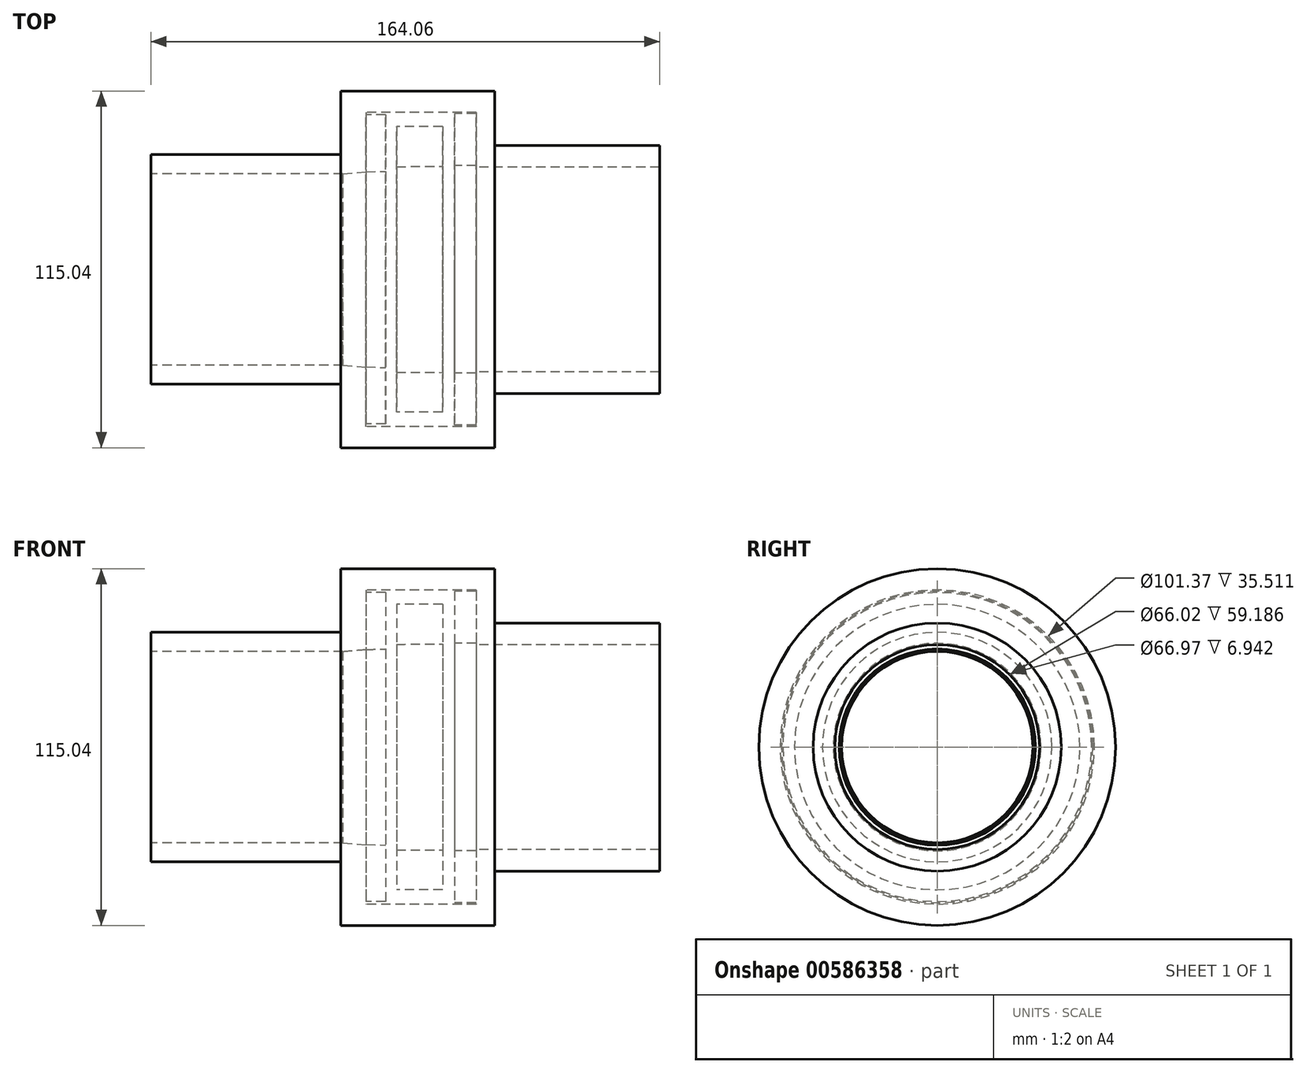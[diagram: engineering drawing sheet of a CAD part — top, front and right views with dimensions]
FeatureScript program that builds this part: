
annotation { "Feature Type Name" : "Feature", "Feature Type Description" : "" }
export const myFeature = defineFeature(function(context is Context, id is Id, definition is map)
    precondition{}
    {
        {
            var Q0;
            Q0=qCreatedBy(makeId("Front.planeOp"),FACE);
            var sketch = newSketch(context, id + "F0", { "sketchPlane" : qUnion([Q0])});
            skLineSegment(sketch, "E0", {"start": v(-67.02, 0) * mm, "end": v(-7.5, 0) * mm});
            skLineSegment(sketch, "E1", {"start": v(-7.5, 0) * mm, "end": v(-7.5, 30.84) * mm});
            skLineSegment(sketch, "E2", {"start": v(-7.5, 30.84) * mm, "end": v(-69.36, 30.84) * mm});
            skLineSegment(sketch, "E3", {"start": v(-69.36, 30.84) * mm, "end": v(-69.36, 37.01) * mm});
            skLineSegment(sketch, "E4", {"start": v(-69.36, 37.01) * mm, "end": v(-8.17, 37.01) * mm});
            skLineSegment(sketch, "E5", {"start": v(-8.17, 37.01) * mm, "end": v(-8.17, 57.52) * mm});
            skLineSegment(sketch, "E6", {"start": v(-8.17, 57.52) * mm, "end": v(41.51, 57.52) * mm});
            skLineSegment(sketch, "E7", {"start": v(41.51, 57.52) * mm, "end": v(41.51, 40.01) * mm});
            skLineSegment(sketch, "E8", {"start": v(41.51, 40.01) * mm, "end": v(94.7, 40.01) * mm});
            skLineSegment(sketch, "E9", {"start": v(94.7, 40.01) * mm, "end": v(94.7, 33.01) * mm});
            skLineSegment(sketch, "E10", {"start": v(94.7, 33.01) * mm, "end": v(35.51, 33.01) * mm});
            skLineSegment(sketch, "E11", {"start": v(35.51, 33.01) * mm, "end": v(35.51, 50.68) * mm});
            skLineSegment(sketch, "E12", {"start": v(35.51, 50.68) * mm, "end": v(0, 50.68) * mm});
            skLineSegment(sketch, "E13", {"start": v(0, 50.68) * mm, "end": v(0, 31.51) * mm});
            skLineSegment(sketch, "E14", {"start": v(0, 31.51) * mm, "end": v(-7.5, 30.84) * mm});
            skSolve(sketch);
        }
        {
            var Q0;
            Q0=qCreatedBy(makeId("Front.planeOp"),FACE);
            var sketch = newSketch(context, id + "F1", { "sketchPlane" : qUnion([Q0])});
            skLineSegment(sketch, "E15", {"start": v(0, 31.45) * mm, "end": v(0, 49.82) * mm});
            skLineSegment(sketch, "E16", {"start": v(0, 49.82) * mm, "end": v(6.33, 49.82) * mm});
            skLineSegment(sketch, "E17", {"start": v(6.33, 49.82) * mm, "end": v(6.33, 31.65) * mm});
            skLineSegment(sketch, "E18", {"start": v(6.33, 31.65) * mm, "end": v(0, 31.45) * mm});
            skSolve(sketch);
        }
        {
            var Q0;
            Q0=qCreatedBy(makeId("Front.planeOp"),FACE);
            var sketch = newSketch(context, id + "F2", { "sketchPlane" : qUnion([Q0])});
            skLineSegment(sketch, "E19", {"start": v(35.53, 33.49) * mm, "end": v(28.59, 33.49) * mm});
            skLineSegment(sketch, "E20", {"start": v(28.59, 33.49) * mm, "end": v(28.59, 50.23) * mm});
            skLineSegment(sketch, "E21", {"start": v(28.59, 50.23) * mm, "end": v(35.53, 50.23) * mm});
            skLineSegment(sketch, "E22", {"start": v(35.53, 50.23) * mm, "end": v(35.53, 33.49) * mm});
            skSolve(sketch);
        }
        {
            var Q0;
            Q0=qCreatedBy(makeId("Front.planeOp"),FACE);
            var sketch = newSketch(context, id + "F3", { "sketchPlane" : qUnion([Q0])});
            skLineSegment(sketch, "E23", {"start": v(9.81, 33.16) * mm, "end": v(9.81, 46.05) * mm});
            skLineSegment(sketch, "E24", {"start": v(9.81, 46.05) * mm, "end": v(24.69, 46.05) * mm});
            skLineSegment(sketch, "E25", {"start": v(24.69, 46.05) * mm, "end": v(24.69, 33.24) * mm});
            skLineSegment(sketch, "E26", {"start": v(24.69, 33.24) * mm, "end": v(9.81, 33.16) * mm});
            skSolve(sketch);
        }
        {
            var Q0;
            Q0 = qSketchRegion(id + "F3", true);
            var Q1;
            Q1=sQuery(id+"F0.wireOp",EDGE,"E0");
            revolve(context, id + "F4", {"entities" : qUnion([Q0]), "axis" : qUnion([Q1]), "revolveType" : RevolveType.FULL});
        }
        {
            var Q0;
            Q0 = qSketchRegion(id + "F2", true);
            var Q1;
            Q1=sQuery(id+"F0.wireOp",EDGE,"E0");
            revolve(context, id + "F5", {"entities" : qUnion([Q0]), "axis" : qUnion([Q1]), "revolveType" : RevolveType.FULL});
        }
        {
            var Q0;
            Q0 = qSketchRegion(id + "F1", true);
            var Q1;
            Q1=sQuery(id+"F0.wireOp",EDGE,"E0");
            revolve(context, id + "F6", {"entities" : qUnion([Q0]), "axis" : qUnion([Q1]), "revolveType" : RevolveType.FULL});
        }
        {
            var Q0;
            Q0 = qSketchRegion(id + "F0", true);
            var Q1;
            Q1=sQuery(id+"F0.wireOp",EDGE,"E0");
            revolve(context, id + "F7", {"entities" : qUnion([Q0]), "axis" : qUnion([Q1]), "revolveType" : RevolveType.FULL});
        }
    });
